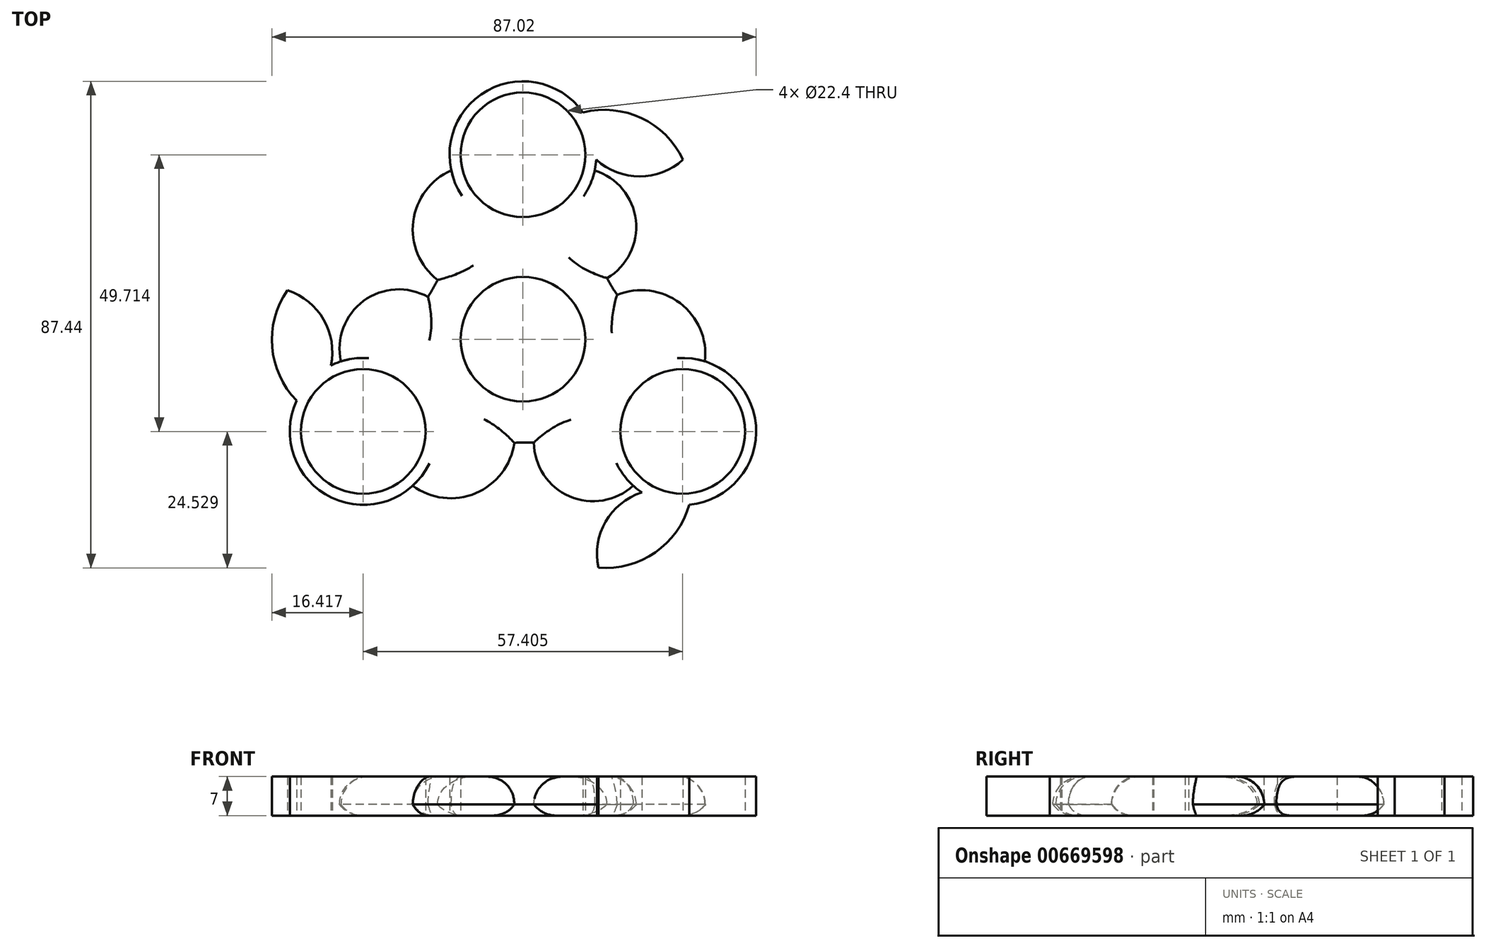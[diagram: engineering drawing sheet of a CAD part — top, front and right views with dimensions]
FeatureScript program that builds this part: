
annotation { "Feature Type Name" : "Feature", "Feature Type Description" : "" }
export const myFeature = defineFeature(function(context is Context, id is Id, definition is map)
    precondition{}
    {
        {
            var Q0;
            Q0=qCreatedBy(makeId("Top.planeOp"),FACE);
            var sketch = newSketch(context, id + "F0", { "sketchPlane" : qUnion([Q0])});
            skCircle(sketch, "E0", {"center": v(0, 0) * mm, "radius": 11.2 * mm});
            skCircle(sketch, "E1", {"center": v(0, 0) * mm, "radius": 13.2 * mm});
            skCircle(sketch, "E2", {"center": v(0, 33.14) * mm, "radius": 11.2 * mm});
            skCircle(sketch, "E3", {"center": v(0, 33.14) * mm, "radius": 13.2 * mm});
            skCircle(sketch, "E4.1.0", {"center": v(-28.7, -16.57) * mm, "radius": 11.2 * mm});
            skCircle(sketch, "E4.1.1", {"center": v(-28.7, -16.57) * mm, "radius": 13.2 * mm});
            skCircle(sketch, "E4.2.0", {"center": v(28.7, -16.57) * mm, "radius": 11.2 * mm});
            skCircle(sketch, "E4.2.1", {"center": v(28.7, -16.57) * mm, "radius": 13.2 * mm});
            skArc(sketch, "E5", {"start": v(-29.33, -3.39) * mm, "mid": v(-15.35, 10.65) * mm, "end": v(-12.9, 30.32) * mm});
            skArc(sketch, "E6.1.0", {"start": v(17.6, -23.7) * mm, "mid": v(-1.55, -18.62) * mm, "end": v(-19.8, -26.32) * mm});
            skArc(sketch, "E6.2.0", {"start": v(11.73, 27.1) * mm, "mid": v(16.9, 7.97) * mm, "end": v(32.7, -4) * mm});
            skArc(sketch, "E7", {"start": v(-12.9, 30.32) * mm, "mid": v(-19.72, 21.18) * mm, "end": v(-15.35, 10.65) * mm});
            skArc(sketch, "E8", {"start": v(15.1, 10.99) * mm, "mid": v(20.27, 21.37) * mm, "end": v(12.9, 30.32) * mm});
            skArc(sketch, "E9.1.0", {"start": v(-17.07, 7.59) * mm, "mid": v(-28.65, 6.87) * mm, "end": v(-32.7, -4) * mm});
            skArc(sketch, "E9.1.1", {"start": v(-19.8, -26.32) * mm, "mid": v(-8.49, -27.67) * mm, "end": v(-1.55, -18.62) * mm});
            skArc(sketch, "E9.2.0", {"start": v(1.96, -18.58) * mm, "mid": v(8.37, -28.24) * mm, "end": v(19.8, -26.32) * mm});
            skArc(sketch, "E9.2.1", {"start": v(32.7, -4) * mm, "mid": v(28.2, 6.48) * mm, "end": v(16.9, 7.97) * mm});
            skArc(sketch, "E10", {"start": v(28.76, 32.27) * mm, "mid": v(21.3, 39.73) * mm, "end": v(10.8, 40.74) * mm});
            skArc(sketch, "E11", {"start": v(13.17, 32.27) * mm, "mid": v(20.97, 29.24) * mm, "end": v(28.76, 32.27) * mm});
            skArc(sketch, "E12.1.0", {"start": v(-42.33, 8.78) * mm, "mid": v(-45.06, -1.42) * mm, "end": v(-40.68, -11.02) * mm});
            skArc(sketch, "E12.1.1", {"start": v(-34.53, -4.73) * mm, "mid": v(-35.8, 3.54) * mm, "end": v(-42.33, 8.78) * mm});
            skArc(sketch, "E12.2.0", {"start": v(13.56, -41.04) * mm, "mid": v(23.76, -38.32) * mm, "end": v(29.89, -29.72) * mm});
            skArc(sketch, "E12.2.1", {"start": v(21.36, -27.54) * mm, "mid": v(14.84, -32.78) * mm, "end": v(13.56, -41.04) * mm});
            skSolve(sketch);
        }
        {
            var Q0;
            Q0=makeQuery(id+"F0.imprint","IMPRINT",FACE,{"disambiguationData":[TD([[makeQuery(id+"F0.imprint","IMPRINT",EDGE,{"derivedFrom":sQuery(id+"F0.wireOp",EDGE,"E1")}),-1.0]])]});
            var Q1;
            Q1=makeQuery(id+"F0.imprint","IMPRINT",FACE,{"disambiguationData":[TD([[makeQuery(id+"F0.imprint","IMPRINT",EDGE,{"derivedFrom":sQuery(id+"F0.wireOp",EDGE,"E0")}),-1.0]])]});
            var Q2;
            {var subQ3=sQuery(id+"F0.wireOp",EDGE,"E8");Q2=makeQuery(id+"F0.imprint","IMPRINT",FACE,{"disambiguationData":[TD([[makeQuery(id+"F0.imprint","IMPRINT",EDGE,{"derivedFrom":subQ3}),1.0]])]});}
            var Q3;
            {var subQ0=sQuery(id+"F0.wireOp",EDGE,"E10");Q3=makeQuery(id+"F0.imprint","IMPRINT",FACE,{"disambiguationData":[TD([[makeQuery(id+"F0.imprint","IMPRINT",EDGE,{"derivedFrom":subQ0}),1.0]])]});}
            var Q4;
            {var subQ0=sQuery(id+"F0.wireOp",EDGE,"E7");Q4=makeQuery(id+"F0.imprint","IMPRINT",FACE,{"disambiguationData":[TD([[makeQuery(id+"F0.imprint","IMPRINT",EDGE,{"derivedFrom":subQ0}),1.0]])]});}
            var Q5;
            Q5=makeQuery(id+"F0.imprint","IMPRINT",FACE,{"disambiguationData":[TD([[makeQuery(id+"F0.imprint","IMPRINT",EDGE,{"derivedFrom":sQuery(id+"F0.wireOp",EDGE,"E2")}),-1.0]])]});
            var Q6;
            {var subQ0=sQuery(id+"F0.wireOp",EDGE,"E9.2.1");Q6=makeQuery(id+"F0.imprint","IMPRINT",FACE,{"disambiguationData":[TD([[makeQuery(id+"F0.imprint","IMPRINT",EDGE,{"derivedFrom":subQ0}),1.0]])]});}
            var Q7;
            {var subQ3=sQuery(id+"F0.wireOp",EDGE,"E9.2.0");Q7=makeQuery(id+"F0.imprint","IMPRINT",FACE,{"disambiguationData":[TD([[makeQuery(id+"F0.imprint","IMPRINT",EDGE,{"derivedFrom":subQ3}),1.0]])]});}
            var Q8;
            {var subQ0=sQuery(id+"F0.wireOp",EDGE,"E12.2.0");Q8=makeQuery(id+"F0.imprint","IMPRINT",FACE,{"disambiguationData":[TD([[makeQuery(id+"F0.imprint","IMPRINT",EDGE,{"derivedFrom":subQ0}),1.0]])]});}
            var Q9;
            {var subQ0=sQuery(id+"F0.wireOp",EDGE,"E9.1.1");Q9=makeQuery(id+"F0.imprint","IMPRINT",FACE,{"disambiguationData":[TD([[makeQuery(id+"F0.imprint","IMPRINT",EDGE,{"derivedFrom":subQ0}),1.0]])]});}
            var Q10;
            {var subQ3=sQuery(id+"F0.wireOp",EDGE,"E9.1.0");Q10=makeQuery(id+"F0.imprint","IMPRINT",FACE,{"disambiguationData":[TD([[makeQuery(id+"F0.imprint","IMPRINT",EDGE,{"derivedFrom":subQ3}),1.0]])]});}
            var Q11;
            {var subQ0=sQuery(id+"F0.wireOp",EDGE,"E12.1.0");Q11=makeQuery(id+"F0.imprint","IMPRINT",FACE,{"disambiguationData":[TD([[makeQuery(id+"F0.imprint","IMPRINT",EDGE,{"derivedFrom":subQ0}),1.0]])]});}
            var Q12;
            Q12=makeQuery(id+"F0.imprint","IMPRINT",FACE,{"disambiguationData":[TD([[makeQuery(id+"F0.imprint","IMPRINT",EDGE,{"derivedFrom":sQuery(id+"F0.wireOp",EDGE,"E4.1.0")}),-1.0]])]});
            var Q13;
            Q13=makeQuery(id+"F0.imprint","IMPRINT",FACE,{"disambiguationData":[TD([[makeQuery(id+"F0.imprint","IMPRINT",EDGE,{"derivedFrom":sQuery(id+"F0.wireOp",EDGE,"E4.2.0")}),-1.0]])]});
            extrude(context, id + "F1", {"entities" : qUnion([Q0, Q1, Q2, Q3, Q4, Q5, Q6, Q7, Q8, Q9, Q10, Q11, Q12, Q13]), "depth" : 7 * mm, "offsetDistance" : 25 * mm});
        }
        {
            var Q0;
            Q0=makeQuery(id+"F1.opExtrude","CAP_EDGE",EDGE,{"disambiguationData":[OSD([sQuery(id+"F0.wireOp",EDGE,"E7")])],"isStart":false});
            var Q1;
            Q1=makeQuery(id+"F1.opExtrude","CAP_EDGE",EDGE,{"disambiguationData":[OSD([sQuery(id+"F0.wireOp",EDGE,"E8")])],"isStart":false});
            var Q2;
            Q2=makeQuery(id+"F1.opExtrude","CAP_EDGE",EDGE,{"disambiguationData":[OSD([sQuery(id+"F0.wireOp",EDGE,"E9.2.1")])],"isStart":false});
            var Q3;
            Q3=makeQuery(id+"F1.opExtrude","CAP_EDGE",EDGE,{"disambiguationData":[OSD([sQuery(id+"F0.wireOp",EDGE,"E9.1.0")])],"isStart":false});
            var Q4;
            Q4=makeQuery(id+"F1.opExtrude","CAP_EDGE",EDGE,{"disambiguationData":[OSD([sQuery(id+"F0.wireOp",EDGE,"E9.1.1")])],"isStart":false});
            var Q5;
            Q5=makeQuery(id+"F1.opExtrude","CAP_EDGE",EDGE,{"disambiguationData":[OSD([sQuery(id+"F0.wireOp",EDGE,"E9.2.0")])],"isStart":false});
            var Q6;
            Q6=makeQuery(id+"F1.opExtrude","CAP_EDGE",EDGE,{"disambiguationData":[OSD([sQuery(id+"F0.wireOp",EDGE,"E6.1.0")])],"isStart":false});
            var Q7;
            Q7=makeQuery(id+"F1.opExtrude","CAP_EDGE",EDGE,{"disambiguationData":[OSD([sQuery(id+"F0.wireOp",EDGE,"E6.2.0")])],"isStart":false});
            var Q8;
            Q8=makeQuery(id+"F1.opExtrude","CAP_EDGE",EDGE,{"disambiguationData":[OSD([sQuery(id+"F0.wireOp",EDGE,"E5")])],"isStart":false});
            fillet(context, id + "F2", {"entities" : qUnion([Q0, Q1, Q2, Q3, Q4, Q5, Q6, Q7, Q8]), "radius" : 5 * mm, "tangentPropagation" : true, "allowEdgeOverflow" : false});
        }
        {
            var Q0;
            Q0=makeQuery(id+"F1.opExtrude","CAP_EDGE",EDGE,{"disambiguationData":[OSD([sQuery(id+"F0.wireOp",EDGE,"E9.1.0")])],"isStart":true});
            var Q1;
            Q1=makeQuery(id+"F1.opExtrude","CAP_EDGE",EDGE,{"disambiguationData":[OSD([sQuery(id+"F0.wireOp",EDGE,"E9.1.1")])],"isStart":true});
            var Q2;
            Q2=makeQuery(id+"F1.opExtrude","CAP_EDGE",EDGE,{"disambiguationData":[OSD([sQuery(id+"F0.wireOp",EDGE,"E9.2.0")])],"isStart":true});
            var Q3;
            Q3=makeQuery(id+"F1.opExtrude","CAP_EDGE",EDGE,{"disambiguationData":[OSD([sQuery(id+"F0.wireOp",EDGE,"E6.1.0")])],"isStart":true});
            var Q4;
            Q4=makeQuery(id+"F1.opExtrude","CAP_EDGE",EDGE,{"disambiguationData":[OSD([sQuery(id+"F0.wireOp",EDGE,"E6.2.0")])],"isStart":true});
            var Q5;
            Q5=makeQuery(id+"F1.opExtrude","CAP_EDGE",EDGE,{"disambiguationData":[OSD([sQuery(id+"F0.wireOp",EDGE,"E5")])],"isStart":true});
            var Q6;
            Q6=makeQuery(id+"F1.opExtrude","CAP_EDGE",EDGE,{"disambiguationData":[OSD([sQuery(id+"F0.wireOp",EDGE,"E7")])],"isStart":true});
            var Q7;
            Q7=makeQuery(id+"F1.opExtrude","CAP_EDGE",EDGE,{"disambiguationData":[OSD([sQuery(id+"F0.wireOp",EDGE,"E8")])],"isStart":true});
            var Q8;
            Q8=makeQuery(id+"F1.opExtrude","CAP_EDGE",EDGE,{"disambiguationData":[OSD([sQuery(id+"F0.wireOp",EDGE,"E9.2.1")])],"isStart":true});
            fillet(context, id + "F3", {"entities" : qUnion([Q0, Q1, Q2, Q3, Q4, Q5, Q6, Q7, Q8]), "radius" : 5 * mm, "tangentPropagation" : true, "allowEdgeOverflow" : false});
        }
    });
